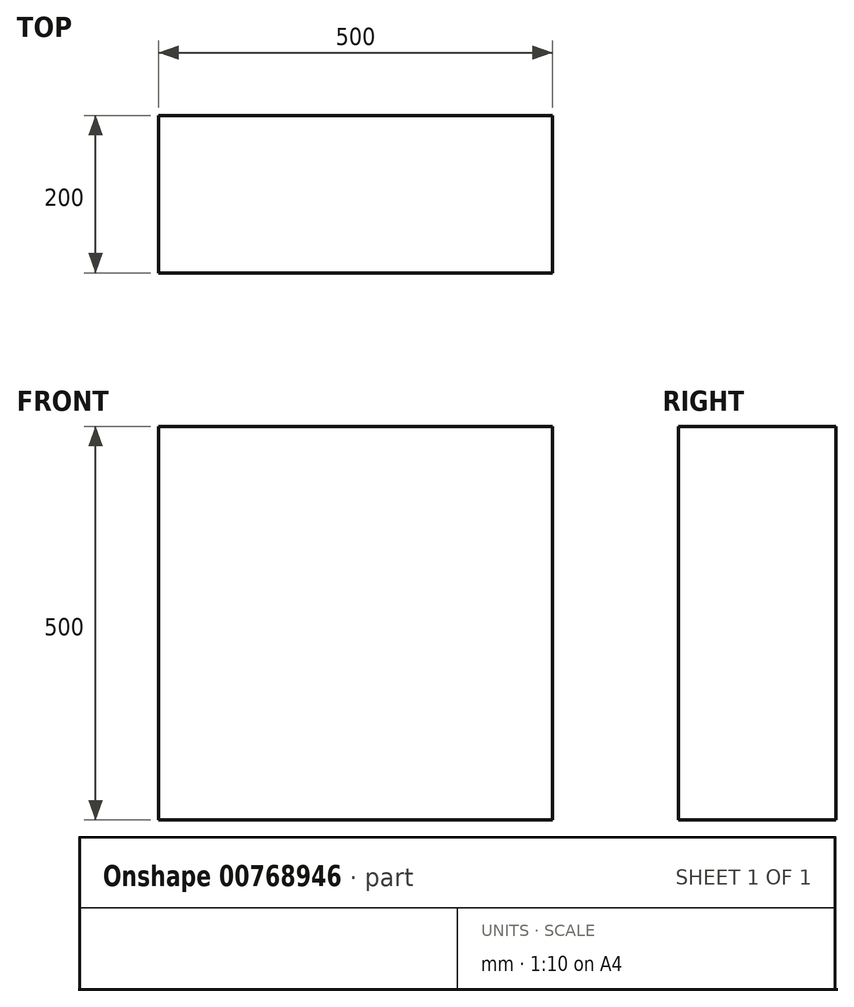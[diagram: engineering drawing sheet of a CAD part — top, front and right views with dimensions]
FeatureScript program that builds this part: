
annotation { "Feature Type Name" : "Feature", "Feature Type Description" : "" }
export const myFeature = defineFeature(function(context is Context, id is Id, definition is map)
    precondition{}
    {
        {
            var Q0;
            Q0=qCreatedBy(makeId("Top.planeOp"),FACE);
            var sketch = newSketch(context, id + "F0", { "sketchPlane" : qUnion([Q0])});
            skLineSegment(sketch, "E0.bottom", {"start": v(-284.27, 57.19) * mm, "end": v(215.73, 57.19) * mm});
            skLineSegment(sketch, "E0.top", {"start": v(-284.27, -142.81) * mm, "end": v(215.73, -142.81) * mm});
            skLineSegment(sketch, "E0.left", {"start": v(-284.27, 57.19) * mm, "end": v(-284.27, -142.81) * mm});
            skLineSegment(sketch, "E0.right", {"start": v(215.73, 57.19) * mm, "end": v(215.73, -142.81) * mm});
            skSolve(sketch);
        }
        {
            var Q0;
            Q0=makeQuery(id+"F0.imprint","IMPRINT",FACE,{"disambiguationData":[TD([[makeQuery(id+"F0.imprint","IMPRINT",EDGE,{"derivedFrom":sQuery(id+"F0.wireOp",EDGE,"E0.bottom")}),-1.0]])]});
            extrude(context, id + "F1", {"entities" : qUnion([Q0]), "depth" : 500 * mm, "offsetDistance" : 25.4 * mm});
        }
    });
